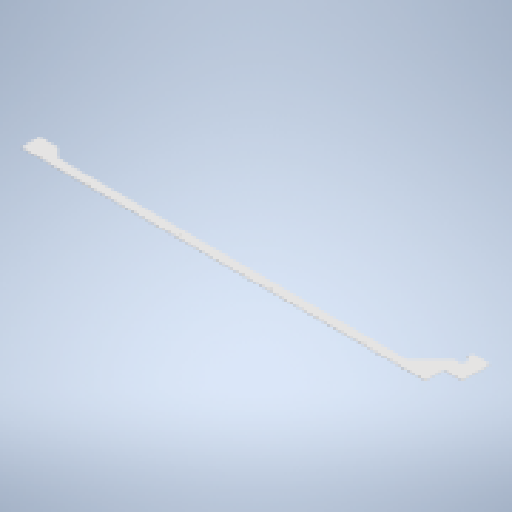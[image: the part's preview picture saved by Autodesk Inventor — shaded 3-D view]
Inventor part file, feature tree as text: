
AUTODESK INVENTOR PART (.ipt)
format: ipt  version: 2025 (Build 290162010, 162A)  size: 334,848 bytes
history: native  units: mm
features: sketch x4, other x3, extrude x2, sheet_metal_op x1, mirror x1, pattern_linear x1
ambient origin geometry x8: Origin, YZ Plane, XZ Plane, XY Plane, X Axis, Y Axis, Z Axis, Center Point
bodies: Solid1 (feature_tree)
feature tree (12):
  sheet_metal_op  "Face1"
  extrude  "Extrusion1"  Depth=3.2mm
  mirror  "Mirror2"
  pattern_linear  "Rectangular Pattern3"  Spacing1=0.0mm  [1 undecoded]
  other  "Mark1"
  extrude  "Extrusion2"  Depth=50.0mm
  sketch  "Sketch1"  dims[d2=3.0mm]
  other  "Plate1"
  sketch  "Sketch2"  dims[d3=2400.0mm d4=2900.0mm d5=50.0mm d6=100.0mm d7=50.0mm d8=2644.536997mm d9=135.0deg d10=949.536997mm d11=1149.536997mm d12=23.747141mm d13=50.0mm d14=100.0mm d15=212.786819mm d16=2700.0mm d17=55.0mm d18=200.0mm d19=200.0mm d20=3.2mm]
  sketch  "Sketch3"  dims[d21=26.0mm]
  sketch  "Sketch4"  dims[d22=748.5mm d23=0.0mm d24=0.0mm d31=50.0mm d33=500.0mm d37=10.0mm d38=0.0mm]
  other  "Definition1"
note: 1 required parameter value undecoded (feature->parameter linkage not recoverable at this tier; creation-order binding heuristic only, values carry confidence <= 0.55)
